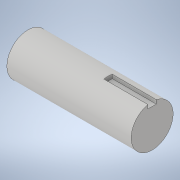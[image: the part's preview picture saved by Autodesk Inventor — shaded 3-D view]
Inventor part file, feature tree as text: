
AUTODESK INVENTOR PART (.ipt)
format: ipt  version: 2021 (Build 250183000, 183)  size: 105,984 bytes
history: native  units: in
note: dims shown in document units (in); Inventor stores cm internally (conversion verified against a paired STEP export)
features: extrude x2, sketch x2, plane x1
ambient origin geometry x8: Origin, YZ Plane, XZ Plane, XY Plane, X Axis, Y Axis, Z Axis, Center Point
bodies: Solid1 (feature_tree)
feature tree (5):
  extrude  "Extrusion1"  Depth=3.7in TaperAngle=0.0deg
  plane  "Work Plane1"
  extrude  "Extrusion9"  Depth=0.25in
  sketch  "Sketch1"  dims[d0=1.25in d1=3.7in d2=0.0in]
  sketch  "Sketch9"  dims[d11=-2.0535in d26=0.25in d27=0.125in d28=1.313in d29=0.0in]
